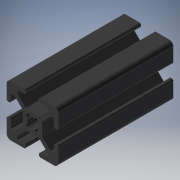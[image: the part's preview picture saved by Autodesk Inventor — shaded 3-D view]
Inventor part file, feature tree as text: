
AUTODESK INVENTOR PART (.ipt)
format: ipt  version: 2019 (Build 230136000, 136)  size: 235,520 bytes
history: native  units: mm
features: extrude x1, sketch x1
ambient origin geometry x8: Origin, YZ Plane, XZ Plane, XY Plane, X Axis, Y Axis, Z Axis, Center Point
bodies: Solid1 (feature_tree)
feature tree (2):
  extrude  "Extrusion1"  [1 undecoded]
  sketch  "Sketch_1"  dims[d0=45.0mm d1=0.0mm]
note: 1 required parameter value undecoded (feature->parameter linkage not recoverable at this tier; creation-order binding heuristic only, values carry confidence <= 0.55)
